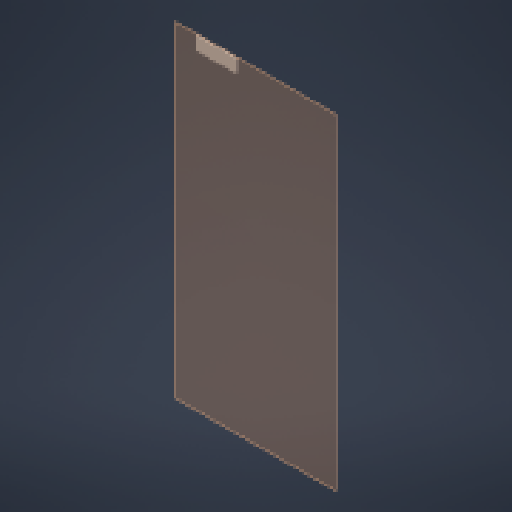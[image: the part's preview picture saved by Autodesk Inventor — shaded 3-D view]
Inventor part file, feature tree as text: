
AUTODESK INVENTOR PART (.ipt)
format: ipt  version: 2024 (Build 280153000, 153)  size: 125,440 bytes
history: native  units: mm
features: other x5, plane x1, extrude x1, sketch x1
ambient origin geometry x8: Origin, YZ Plane, XZ Plane, XY Plane, X Axis, Y Axis, Z Axis, Center Point
bodies: Body1 (feature_tree)
feature tree (8):
  other  "Sólido1"
  plane  "Plano de trabajo1"
  extrude  "Extrusión1"  Depth=30.0mm
  sketch  "Boceto1"  dims[d0=120.0mm d1=30.0mm d2=30.0mm d3=30.0mm d4=2.0mm d5=0.0mm]
  other  "<userpath>\Downloads\Piezas CMR\Marco_APM_003\Marco_apm_003-1.iam"
  other  "Marco_apm_003-1.iam"
  other  "Marco_Conveyor_Aereo:1"
  other  "Marco:1"
